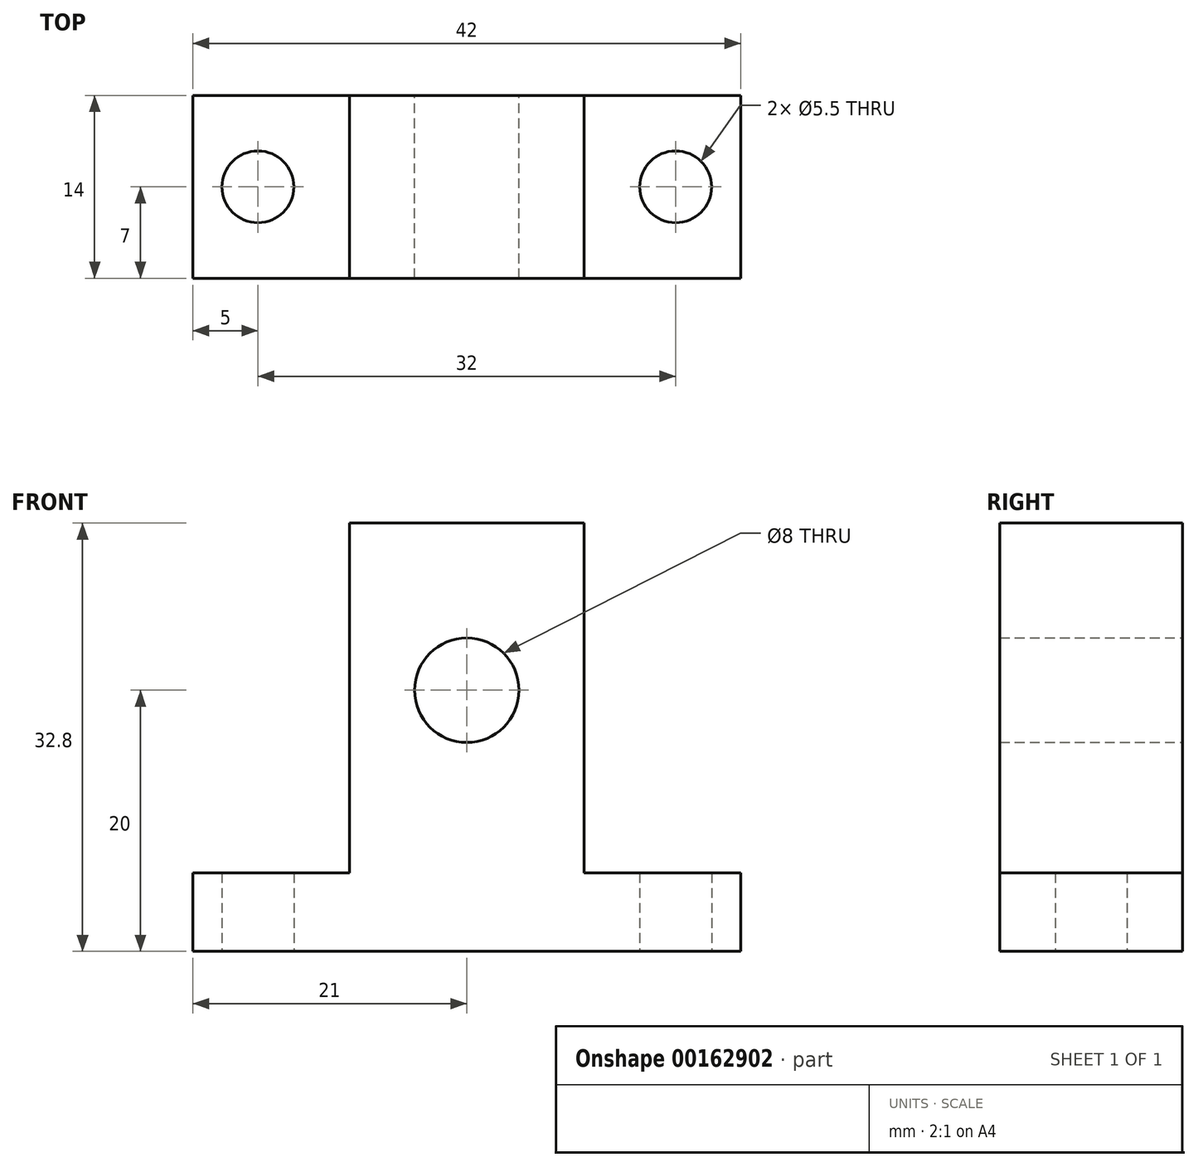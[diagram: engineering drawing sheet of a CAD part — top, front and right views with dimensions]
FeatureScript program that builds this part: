
annotation { "Feature Type Name" : "Feature", "Feature Type Description" : "" }
export const myFeature = defineFeature(function(context is Context, id is Id, definition is map)
    precondition{}
    {
        {
            var Q0;
            Q0=qCreatedBy(makeId("Front.planeOp"),FACE);
            var sketch = newSketch(context, id + "F0", { "sketchPlane" : qUnion([Q0])});
            skLineSegment(sketch, "E0", {"start": v(0, -6) * mm, "end": v(-21, -6) * mm});
            skLineSegment(sketch, "E1", {"start": v(-21, -6) * mm, "end": v(-21, 0) * mm});
            skLineSegment(sketch, "E2", {"start": v(-21, 0) * mm, "end": v(-9, 0) * mm});
            skLineSegment(sketch, "E3", {"start": v(-9, 0) * mm, "end": v(-9, 26.8) * mm});
            skLineSegment(sketch, "E4", {"start": v(-9, 26.8) * mm, "end": v(0, 26.8) * mm});
            skLineSegment(sketch, "E5.MirrorCS", {"start": v(0, -6) * mm, "end": v(21, -6) * mm});
            skLineSegment(sketch, "E6.MirrorCS", {"start": v(21, 0) * mm, "end": v(9, 0) * mm});
            skLineSegment(sketch, "E7.MirrorCS", {"start": v(9, 26.8) * mm, "end": v(0, 26.8) * mm});
            skLineSegment(sketch, "E8.MirrorCS", {"start": v(9, 0) * mm, "end": v(9, 26.8) * mm});
            skLineSegment(sketch, "E9.MirrorCS", {"start": v(21, -6) * mm, "end": v(21, 0) * mm});
            skCircle(sketch, "E10", {"center": v(0, 14) * mm, "radius": 4 * mm});
            skSolve(sketch);
        }
        {
            var Q0;
            Q0=makeQuery(id+"F0.imprint","IMPRINT",FACE,{"disambiguationData":[TD([[makeQuery(id+"F0.imprint","IMPRINT",EDGE,{"derivedFrom":sQuery(id+"F0.wireOp",EDGE,"E0")}),-1.0]])]});
            extrude(context, id + "F1", {"entities" : qUnion([Q0]), "depth" : 14 * mm});
        }
        {
            var Q0;
            Q0=makeQuery(id+"F1.opExtrude","SWEPT_FACE",FACE,{"disambiguationData":[OSD([sQuery(id+"F0.wireOp",EDGE,"E0"),sQuery(id+"F0.wireOp",EDGE,"E5.MirrorCS")])]});
            var sketch = newSketch(context, id + "F2", { "sketchPlane" : qUnion([Q0])});
            skPoint(sketch, "E11", {"position": v(-16, 7) * mm});
            skPoint(sketch, "E11.positionSnap0", {"position": v(-21, 7) * mm});
            skPoint(sketch, "E12.MirrorP", {"position": v(16, 7) * mm});
            skSolve(sketch);
        }
        {
            var Q0;
            Q0=sQuery(id+"F2.wireOp",VERTEX,"E11");
            var Q1;
            Q1=sQuery(id+"F2.wireOp",VERTEX,"E12.MirrorP");
            var Q2;
            Q2=makeQuery(id+"F1.opExtrude","SWEPT_BODY",BODY,{"disambiguationData":[OSD([sQuery(id+"F0.wireOp",EDGE,"E0"),sQuery(id+"F0.wireOp",EDGE,"E1"),sQuery(id+"F0.wireOp",EDGE,"E2"),sQuery(id+"F0.wireOp",EDGE,"E3"),sQuery(id+"F0.wireOp",EDGE,"E4"),sQuery(id+"F0.wireOp",EDGE,"E5.MirrorCS"),sQuery(id+"F0.wireOp",EDGE,"E6.MirrorCS"),sQuery(id+"F0.wireOp",EDGE,"E7.MirrorCS"),sQuery(id+"F0.wireOp",EDGE,"E8.MirrorCS"),sQuery(id+"F0.wireOp",EDGE,"E9.MirrorCS"),sQuery(id+"F0.wireOp",EDGE,"E10")])]});
            hole(context, id + "F3", {"style" : HoleStyle.SIMPLE, "endStyle" : HoleEndStyle.THROUGH, "standardTappedOrClearance" : lookupTablePath({ "standard" : "ISO", "fit" : "Normal", "size" : "M5", "type" : "Clearance" }), "standardBlindInLast" : lookupTablePath({ "fit" : "Standard", "standard" : "ISO", "size" : "M5", "type" : "Clearance" }), "holeDiameter" : 5.5 * mm, "startFromSketch" : true, "locations" : qUnion([Q0, Q1]), "scope" : qUnion([Q2]), "isTappedThrough" : true});
        }
    });
